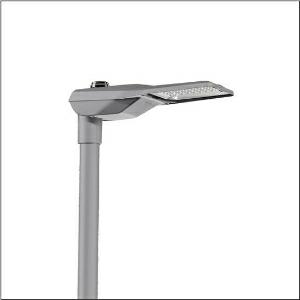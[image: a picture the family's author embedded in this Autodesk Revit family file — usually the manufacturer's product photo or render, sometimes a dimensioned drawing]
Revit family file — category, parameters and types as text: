
# Revit family: streetlight_sl_21_mini___pl52_5xe6h47n08gb_a206
name_source: partatom
category: Lighting Fixtures
units: mm (PartAtom-declared; Revit-internal decimal feet)

## family parameters
Cut with Voids When Loaded = No
Host = Face
Light Source = No
Part Type = Normal
Room Calculation Point = No
Round Connector Dimension = Use Diameter
Shared = No

## types (1)
- --- (1 x LED, 6080 lm, 40.4 W, 4000K)
    Apparent Load = 40 VA
    CIE Flux Codes = 27 59 98 100 100
    Color Rendering = 70
    Color Temperature = 4000K
    Default Elevation = 1800 mm
    Description = Streetlight SL 21 mini, mast luminaire, primary light control with lens, of PMMA, primary optical cover: cover, of toughened safety glass, transparent, light distribution: PL52, light emission: direct distribution, primary light characteristic: asymmetric, installation type: side-entry, LED, 3G 1.5mm², High Power LED, rated luminous flux: 6.080lm, luminous efficacy: 151lm/W, light colour: 740, colour temperature: 4000K, control gear: NEMA (7pin), control: overheat protection, pre-setting: linear dimming characteristic, constant luminous flux control, time-dependent luminous flux control, flexible luminous flux parameterisation, mains connection: 230..240V, AC, 50/60Hz, connection cable pre-assembled, cable length: 8,5m, wiring characteristics: H07RN-F, start of lifetime: 40W, end of service life: 41W, reduction: 19W, luminaire housing, of diecast aluminium (EN AC-44300), powder-coated, SITECO metallic grey (DB 702S), corrosivity category C5 high according to DIN EN ISO 12944, multi-level sealing system, sealing non-destructively replaceable, inclination adjustable: 0°, 5°, 10°, 15°, length: 628mm, width: 235mm, height: 110mm, spigot size: 42mm (side-entry), mounting height: 4..8m, protection rating (complete): IP66, insulation class (complete): insulation class I (protective earthing), certification: CE, ENEC, ENEC+, VDE, impact resistance: IK10, permissible operating ambient temperature for outdoor applications: -40..+50°C, standard-compliant lighting for roads and squares, packaging unit: 1 piece

Light Distribution: PL52
    Height = 110 mm
    Lamp = 1 x LED
    Lamp Light Flux = 6080 lm
    Lamp Power = 40.4 W
    Lamp count = 1
    Length = 625 mm
    Luminous efficacy = 151 lm/W
    Manufacturer = Siteco
    ModVariant = No
    Model = 5XE6H47N08GB
    Number of Poles = 1
    OnlyDefault = Yes
    Power Factor = 1
    Product Name = Streetlight SL 21 mini | PL52
    Product group = mast luminaire | pylon top
    ProductGroupID = 6100
    Protection Class = Protection class I
    Protection Degree = IP 66
    RLX_Detail_Level = 1
    RLX_Emergency_Light_Flux = 0 lm
    RLX_Emergency_Type = 0
    RLX_Emergency_Type_DB = No
    RlxData = <blob elided: 35393 chars, md5=e44e1412>
    Socket = socket
    Standby Power = 0 W
    System Light Flux = 6080 lm
    System Power = 40 W
    Type Comments = factory setting: luminous flux: 100 % | dim-lin: 254 | 812 mA
    Type Image = l_1294379.jpg
    URL = http://relux.com
    VarID = @adj_136501
    Voltage = 0 V
    Weight = 0.00 kg
    Width = 234 mm

## geometry (parser evidence)
native form markers: Blend x4, Sweep x11
no freeform markers — native parametric forms only
